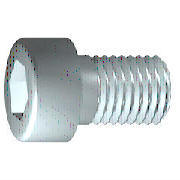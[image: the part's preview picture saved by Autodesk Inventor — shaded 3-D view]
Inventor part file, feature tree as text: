
AUTODESK INVENTOR PART (.ipt)
format: ipt  version: 2022 (Build 260153000, 153)  size: 192,512 bytes
history: native  units: mm (DEFAULTED — no unit token found)
features: sketch x2, extrude x1, plane x1, fillet x1
ambient origin geometry x7: Origin, YZ Plane, XY Plane, X Axis, Y Axis, Z Axis, Center Point
bodies: Solid1 (feature_tree), Body (feature_tree)
feature tree (5):
  extrude  "Slot"  Depth=4.0mm
  plane  "Work Plane1"
  fillet  "Fillet2"  Radius=4.0mm
  sketch  "Sketch1"  dims[d1=14.25mm d2=0.429515mm d3=4.0mm]
  sketch  "Sketch2"  dims[d4=2.0mm d5=60.0deg d6=4.0mm d7=4.0mm d8=3.464102mm d9=7.0mm d10=90.0deg d11=10.0mm d12=0.0mm d13=14.25mm d14=0.0mm d15=0.429415mm d16=0.429415mm d17=0.4mm d19=0.0mm d26=16.0mm d27=45.0deg d28=0.0mm d29=0.0mm d30=0.1mm]
